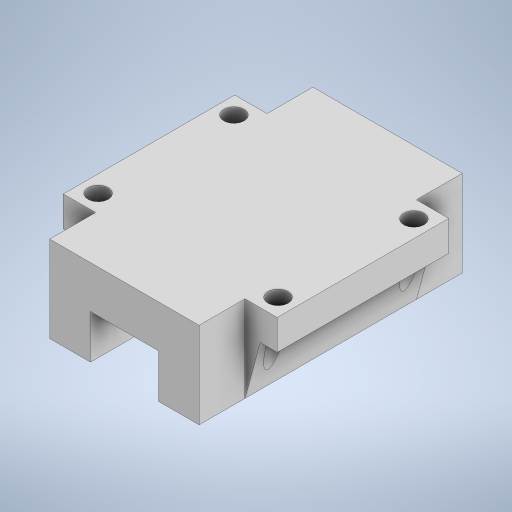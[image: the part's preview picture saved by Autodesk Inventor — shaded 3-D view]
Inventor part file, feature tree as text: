
AUTODESK INVENTOR PART (.ipt)
format: ipt  version: 2023 (Build 270158000, 158)  size: 265,216 bytes
history: native  units: mm
features: extrude x3, sketch x3
ambient origin geometry x8: Origin, YZ Plane, XZ Plane, XY Plane, X Axis, Y Axis, Z Axis, Center Point
bodies: Solid1 (feature_tree)
feature tree (6):
  extrude  "Extrusion1"  Depth=25.4mm
  extrude  "Extrusion2"  Depth=8.9mm
  extrude  "Extrusion3"  Depth=12.0mm
  sketch  "Sketch1"  dims[d0=63.0mm d1=25.4mm]
  sketch  "Sketch2"  dims[d4=21.5mm d5=8.9mm]
  sketch  "Sketch3"  dims[d6=12.9mm d7=12.0mm d8=5.0mm d9=50.5mm d10=0.0mm d11=13.5mm d12=64.0mm d13=0.0mm d14=0.0mm d15=6.0mm d16=40.0mm d17=53.0mm d18=34.5mm d19=0.0mm]
